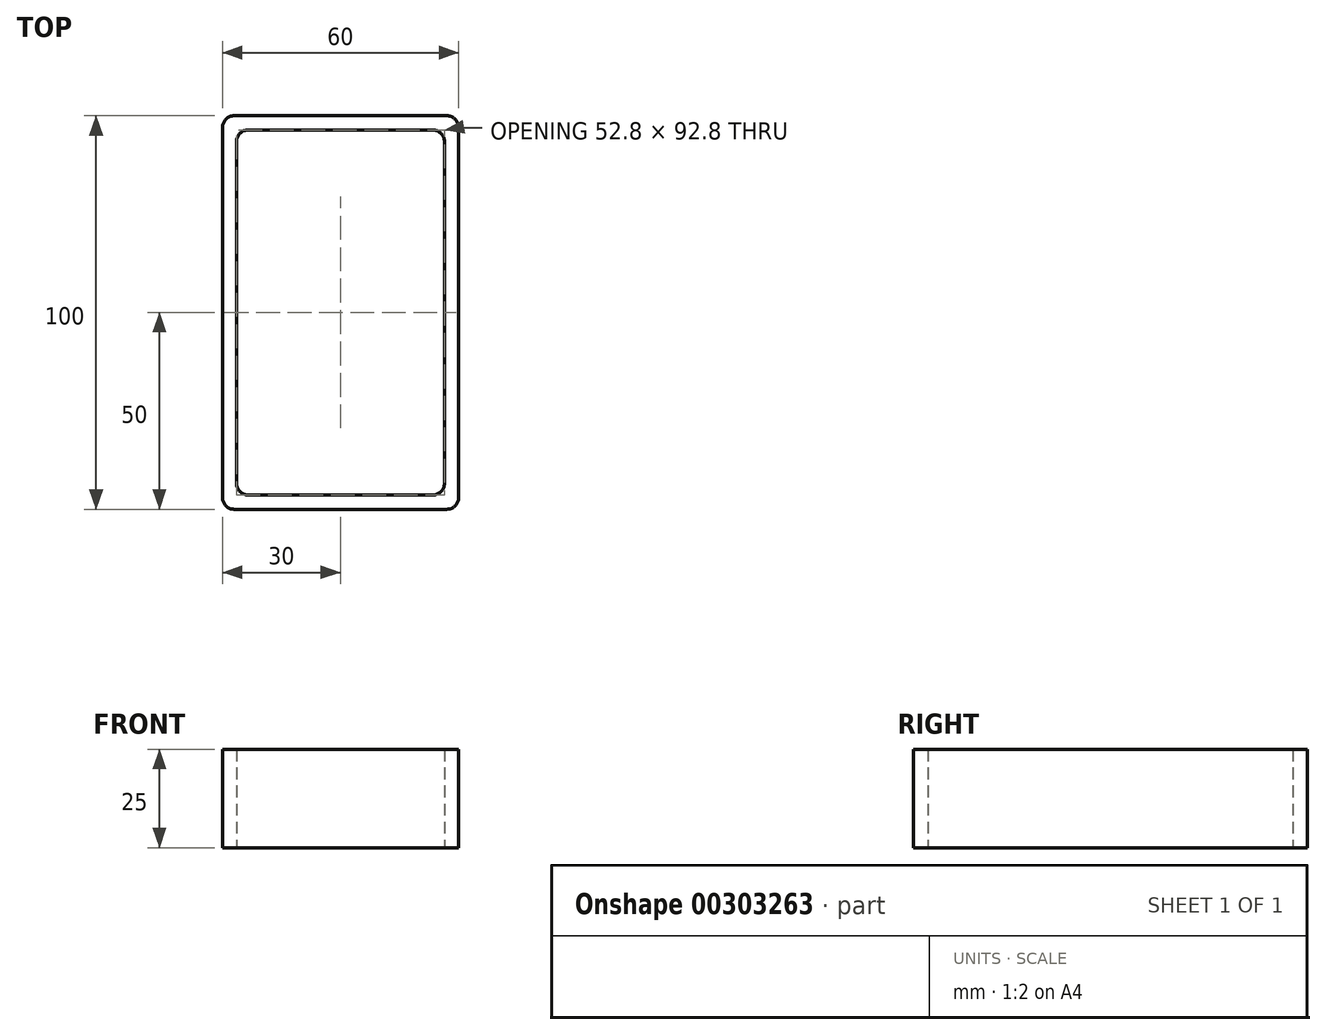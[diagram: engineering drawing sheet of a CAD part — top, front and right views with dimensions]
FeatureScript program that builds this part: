
annotation { "Feature Type Name" : "Feature", "Feature Type Description" : "" }
export const myFeature = defineFeature(function(context is Context, id is Id, definition is map)
    precondition{}
    {
        {
            var Q0;
            Q0=qCreatedBy(makeId("Top.planeOp"),FACE);
            var sketch = newSketch(context, id + "F0", { "sketchPlane" : qUnion([Q0])});
            skLineSegment(sketch, "E0.bottom", {"start": v(3, 0) * mm, "end": v(57, 0) * mm});
            skLineSegment(sketch, "E0.top", {"start": v(3, 100) * mm, "end": v(57, 100) * mm});
            skLineSegment(sketch, "E0.left", {"start": v(0, 3) * mm, "end": v(0, 97) * mm});
            skLineSegment(sketch, "E0.right", {"start": v(60, 3) * mm, "end": v(60, 97) * mm});
            skLineSegment(sketch, "E1.bottom", {"start": v(6.6, 96.4) * mm, "end": v(53.4, 96.4) * mm});
            skLineSegment(sketch, "E1.top", {"start": v(6.6, 3.6) * mm, "end": v(53.4, 3.6) * mm});
            skLineSegment(sketch, "E1.left", {"start": v(3.6, 93.4) * mm, "end": v(3.6, 6.6) * mm});
            skLineSegment(sketch, "E1.right", {"start": v(56.4, 93.4) * mm, "end": v(56.4, 6.6) * mm});
            skPoint(sketch, "E2.visualSharp", {"position": v(0, 100) * mm});
            skArc(sketch, "E2.filletArc", {"start": v(3, 100) * mm, "mid": v(0.88, 99.12) * mm, "end": v(0, 97) * mm});
            skPoint(sketch, "E3.visualSharp", {"position": v(60, 100) * mm});
            skArc(sketch, "E3.filletArc", {"start": v(60, 97) * mm, "mid": v(59.12, 99.12) * mm, "end": v(57, 100) * mm});
            skPoint(sketch, "E4.visualSharp", {"position": v(56.4, 96.4) * mm});
            skArc(sketch, "E4.filletArc", {"start": v(56.4, 93.4) * mm, "mid": v(55.52, 95.52) * mm, "end": v(53.4, 96.4) * mm});
            skPoint(sketch, "E5.visualSharp", {"position": v(3.6, 96.4) * mm});
            skArc(sketch, "E5.filletArc", {"start": v(6.6, 96.4) * mm, "mid": v(4.48, 95.52) * mm, "end": v(3.6, 93.4) * mm});
            skPoint(sketch, "E6.visualSharp", {"position": v(0, 0) * mm});
            skArc(sketch, "E6.filletArc", {"start": v(0, 3) * mm, "mid": v(0.88, 0.88) * mm, "end": v(3, 0) * mm});
            skPoint(sketch, "E7.visualSharp", {"position": v(3.6, 3.6) * mm});
            skArc(sketch, "E7.filletArc", {"start": v(3.6, 6.6) * mm, "mid": v(4.48, 4.48) * mm, "end": v(6.6, 3.6) * mm});
            skPoint(sketch, "E8.visualSharp", {"position": v(56.4, 3.6) * mm});
            skArc(sketch, "E8.filletArc", {"start": v(53.4, 3.6) * mm, "mid": v(55.52, 4.48) * mm, "end": v(56.4, 6.6) * mm});
            skPoint(sketch, "E9.visualSharp", {"position": v(60, 0) * mm});
            skArc(sketch, "E9.filletArc", {"start": v(57, 0) * mm, "mid": v(59.12, 0.88) * mm, "end": v(60, 3) * mm});
            skSolve(sketch);
        }
        {
            var Q0;
            Q0 = qSketchRegion(id + "F0", true);
            extrude(context, id + "F1", {"entities" : qUnion([Q0]), "depth" : 25 * mm});
        }
    });
